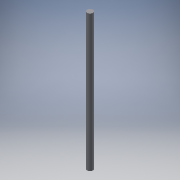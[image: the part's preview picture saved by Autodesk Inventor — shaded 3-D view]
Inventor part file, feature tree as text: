
AUTODESK INVENTOR PART (.ipt)
format: ipt  version: 2018 (Build 220112000, 112)  size: 89,600 bytes
history: native  units: mm
features: other x1, extrude x1, sketch x1
ambient origin geometry x8: Origin, YZ Plane, XZ Plane, XY Plane, X Axis, Y Axis, Z Axis, Center Point
bodies: Body1 (feature_tree)
feature tree (3):
  other  "ソリッド1"
  extrude  "押し出し1"  Depth=12.0mm
  sketch  "スケッチ1"
